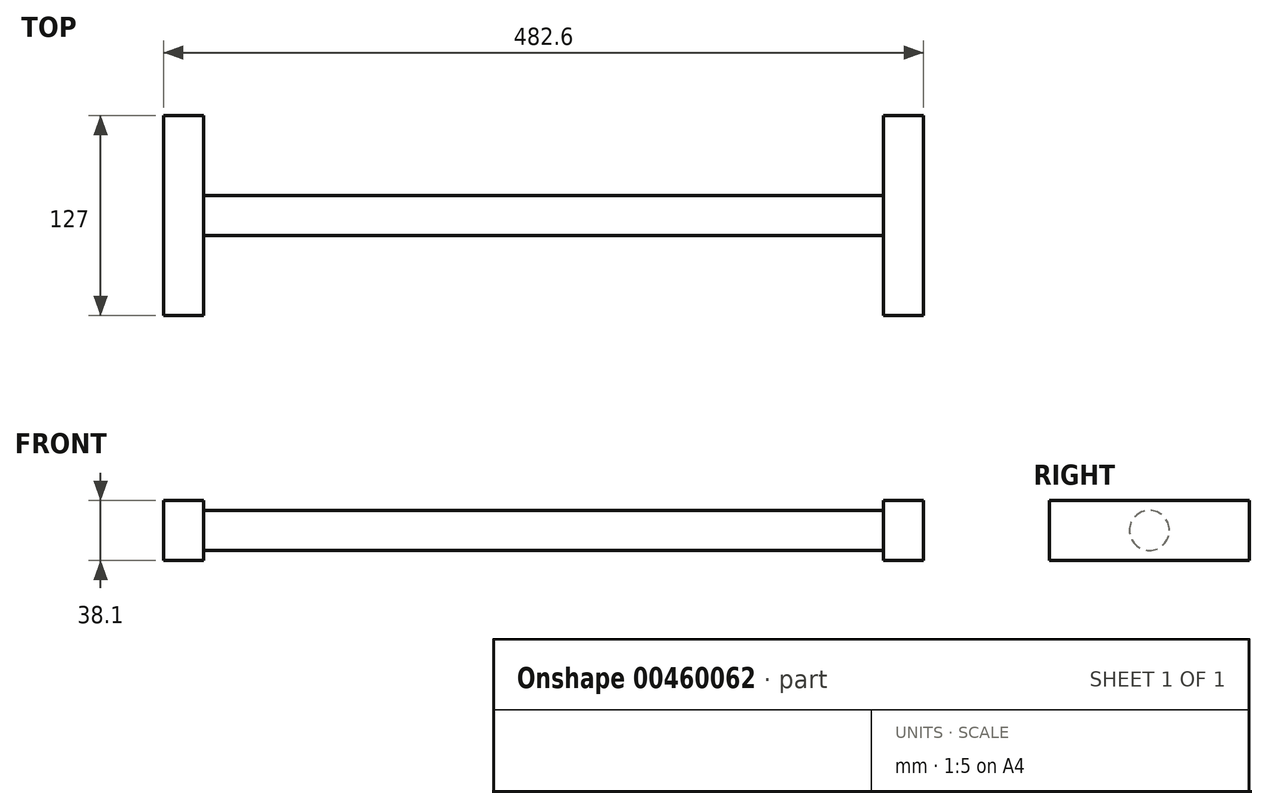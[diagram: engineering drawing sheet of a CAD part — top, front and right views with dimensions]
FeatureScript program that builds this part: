
annotation { "Feature Type Name" : "Feature", "Feature Type Description" : "" }
export const myFeature = defineFeature(function(context is Context, id is Id, definition is map)
    precondition{}
    {
        {
            var Q0;
            Q0=qCreatedBy(makeId("Top.planeOp"),FACE);
            var sketch = newSketch(context, id + "F0", { "sketchPlane" : qUnion([Q0])});
            skLineSegment(sketch, "E0.bottom", {"start": v(-71.7, 91.77) * mm, "end": v(-46.3, 91.77) * mm});
            skLineSegment(sketch, "E0.top", {"start": v(-71.7, -35.23) * mm, "end": v(-46.3, -35.23) * mm});
            skLineSegment(sketch, "E0.left", {"start": v(-71.7, 91.77) * mm, "end": v(-71.7, -35.23) * mm});
            skLineSegment(sketch, "E0.right", {"start": v(-46.3, 91.77) * mm, "end": v(-46.3, -35.23) * mm});
            skLineSegment(sketch, "E1.left", {"start": v(-46.3, 40.97) * mm, "end": v(-46.3, 15.57) * mm});
            skSolve(sketch);
        }
        {
            var Q0;
            Q0=qSketchRegion(id+"F0",true);
            extrude(context, id + "F1", {"entities" : qUnion([Q0]), "depth" : 38.1 * mm});
        }
        {
            var Q0;
            Q0=makeQuery(id+"F1.opExtrude","SWEPT_FACE",FACE,{"disambiguationData":[OSD([sQuery(id+"F0.wireOp",EDGE,"E0.right"),sQuery(id+"F0.wireOp",EDGE,"E1.left")])]});
            var sketch = newSketch(context, id + "F2", { "sketchPlane" : qUnion([Q0])});
            skCircle(sketch, "E2", {"center": v(28.27, 19.05) * mm, "radius": 12.7 * mm});
            skPoint(sketch, "E2.centerSnap0", {"position": v(28.27, 44.45) * mm});
            skPoint(sketch, "E3", {"position": v(28.27, 38.1) * mm});
            skPoint(sketch, "E4", {"position": v(-35.23, 19.05) * mm});
            skSolve(sketch);
        }
        {
            var Q0;
            Q0=qSketchRegion(id+"F2",true);
            extrude(context, id + "F3", {"entities" : qUnion([Q0]), "operationType" : NewBodyOperationType.ADD, "depth" : 431.8 * mm});
        }
        {
            var Q0;
            Q0=makeQuery(id+"F3.opExtrude","CAP_FACE",FACE,{"disambiguationData":[OSD([sQuery(id+"F2.wireOp",EDGE,"E2")])],"isStart":false});
            var sketch = newSketch(context, id + "F4", { "sketchPlane" : qUnion([Q0])});
            skLineSegment(sketch, "E5.bottom", {"start": v(91.77, 38.1) * mm, "end": v(-35.23, 38.1) * mm});
            skLineSegment(sketch, "E5.top", {"start": v(91.77, 0) * mm, "end": v(-35.23, 0) * mm});
            skLineSegment(sketch, "E5.left", {"start": v(91.77, 38.1) * mm, "end": v(91.77, 0) * mm});
            skLineSegment(sketch, "E5.right", {"start": v(-35.23, 38.1) * mm, "end": v(-35.23, 0) * mm});
            skPoint(sketch, "E5.middle", {"position": v(28.27, 19.05) * mm});
            skSolve(sketch);
        }
        {
            var Q0;
            Q0=qSketchRegion(id+"F4",true);
            extrude(context, id + "F5", {"entities" : qUnion([Q0]), "operationType" : NewBodyOperationType.ADD, "depth" : 25.4 * mm});
        }
    });
